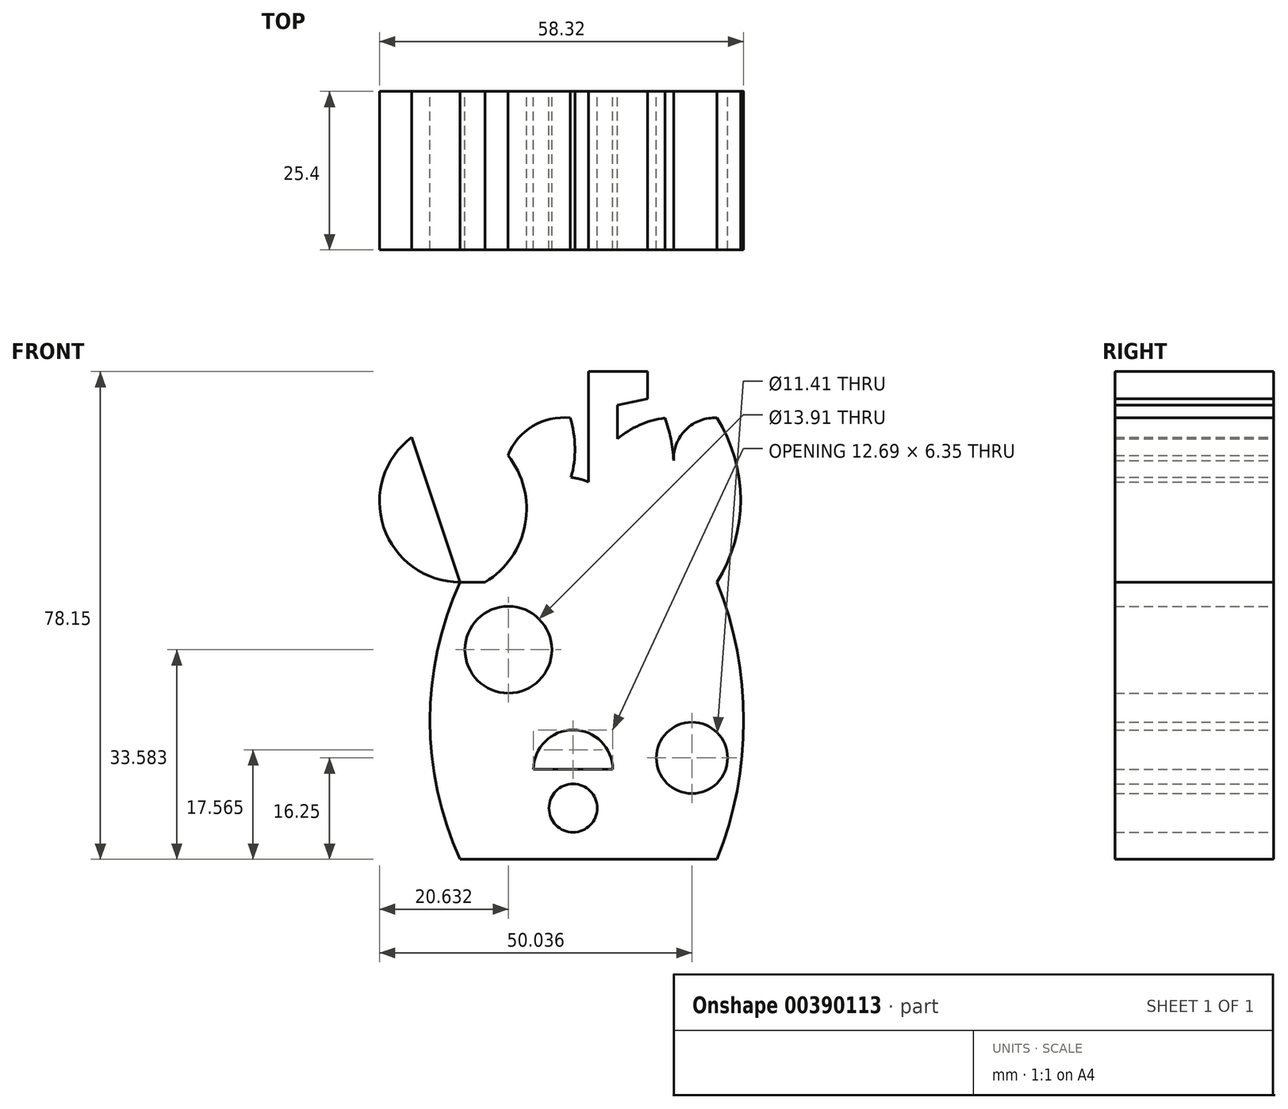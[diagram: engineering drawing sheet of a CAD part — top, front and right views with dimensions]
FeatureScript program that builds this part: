
annotation { "Feature Type Name" : "Feature", "Feature Type Description" : "" }
export const myFeature = defineFeature(function(context is Context, id is Id, definition is map)
    precondition{}
    {
        {
            var Q0;
            Q0=qCreatedBy(makeId("Front.planeOp"),FACE);
            var sketch = newSketch(context, id + "F0", { "sketchPlane" : qUnion([Q0])});
            skLineSegment(sketch, "E0", {"start": v(0, 0) * mm, "end": v(-41.17, 0) * mm});
            skArc(sketch, "E1", {"start": v(-41.17, 44.42) * mm, "mid": v(-45.98, 22.2) * mm, "end": v(-41.17, 0) * mm});
            skArc(sketch, "E2", {"start": v(0, 0) * mm, "mid": v(4.26, 22.2) * mm, "end": v(0, 44.42) * mm});
            skLineSegment(sketch, "E3", {"start": v(-41.17, 44.42) * mm, "end": v(0, 44.42) * mm});
            skArc(sketch, "E4", {"start": v(-48.9, 67.63) * mm, "mid": v(-53.4, 53.23) * mm, "end": v(-41.17, 44.42) * mm});
            skLineSegment(sketch, "E5", {"start": v(-48.9, 67.63) * mm, "end": v(-41.17, 44.42) * mm});
            skArc(sketch, "E6", {"start": v(-45.03, 57.31) * mm, "mid": v(-40.32, 62.06) * mm, "end": v(-37.14, 67.94) * mm});
            skPoint(sketch, "E6.startSnap0", {"position": v(-45.03, 56.02) * mm});
            skArc(sketch, "E7", {"start": v(-37.14, 44.42) * mm, "mid": v(-30.51, 56.18) * mm, "end": v(-37.14, 67.94) * mm});
            skArc(sketch, "E8", {"start": v(-23.52, 70.72) * mm, "mid": v(-29.53, 69.42) * mm, "end": v(-33.5, 64.73) * mm});
            skArc(sketch, "E9", {"start": v(-31.63, 50.75) * mm, "mid": v(-24.03, 59.3) * mm, "end": v(-23.52, 70.72) * mm});
            skArc(sketch, "E10", {"start": v(-20.58, 44.42) * mm, "mid": v(-15.68, 54.47) * mm, "end": v(-24.6, 61.23) * mm});
            skArc(sketch, "E11", {"start": v(-8.36, 70.72) * mm, "mid": v(-15.97, 67.37) * mm, "end": v(-20.58, 60.44) * mm});
            skArc(sketch, "E12", {"start": v(-14.86, 44.42) * mm, "mid": v(-7.62, 56.59) * mm, "end": v(-8.36, 70.72) * mm});
            skArc(sketch, "E13", {"start": v(0, 70.72) * mm, "mid": v(-4.99, 68.86) * mm, "end": v(-6.96, 63.91) * mm});
            skArc(sketch, "E14", {"start": v(0, 44.42) * mm, "mid": v(3.76, 57.57) * mm, "end": v(0, 70.72) * mm});
            skCircle(sketch, "E15", {"center": v(-33.43, 33.58) * mm, "radius": 6.96 * mm});
            skLineSegment(sketch, "E16", {"start": v(-29.4, 0) * mm, "end": v(-29.4, 14.4) * mm});
            skLineSegment(sketch, "E17", {"start": v(-16.71, 14.4) * mm, "end": v(-16.71, 0) * mm});
            skLineSegment(sketch, "E18", {"start": v(-16.71, 0) * mm, "end": v(-16.71, 14.4) * mm});
            skLineSegment(sketch, "E19", {"start": v(-29.4, 14.4) * mm, "end": v(-16.71, 14.4) * mm});
            skArc(sketch, "E20", {"start": v(-16.71, 14.4) * mm, "mid": v(-23.06, 20.74) * mm, "end": v(-29.4, 14.4) * mm});
            skCircle(sketch, "E21", {"center": v(-23.06, 8.2) * mm, "radius": 3.87 * mm});
            skCircle(sketch, "E22", {"center": v(-4.02, 16.25) * mm, "radius": 5.7 * mm});
            skLineSegment(sketch, "E23", {"start": v(-20.58, 60.44) * mm, "end": v(-20.58, 78.15) * mm});
            skLineSegment(sketch, "E24", {"start": v(-20.58, 78.15) * mm, "end": v(-11.14, 78.15) * mm});
            skLineSegment(sketch, "E25", {"start": v(-11.14, 78.15) * mm, "end": v(-11.14, 73.82) * mm});
            skLineSegment(sketch, "E26", {"start": v(-11.14, 73.82) * mm, "end": v(-15.97, 72.8) * mm});
            skPoint(sketch, "E26.endSnap0", {"position": v(-15.97, 67.37) * mm});
            skLineSegment(sketch, "E27", {"start": v(-15.97, 72.8) * mm, "end": v(-15.97, 67.37) * mm});
            skSolve(sketch);
        }
        {
            var Q0;
            Q0 = qSketchRegion(id + "F0", true);
            extrude(context, id + "F1", {"entities" : qUnion([Q0]), "depth" : 25.4 * mm});
        }
    });
